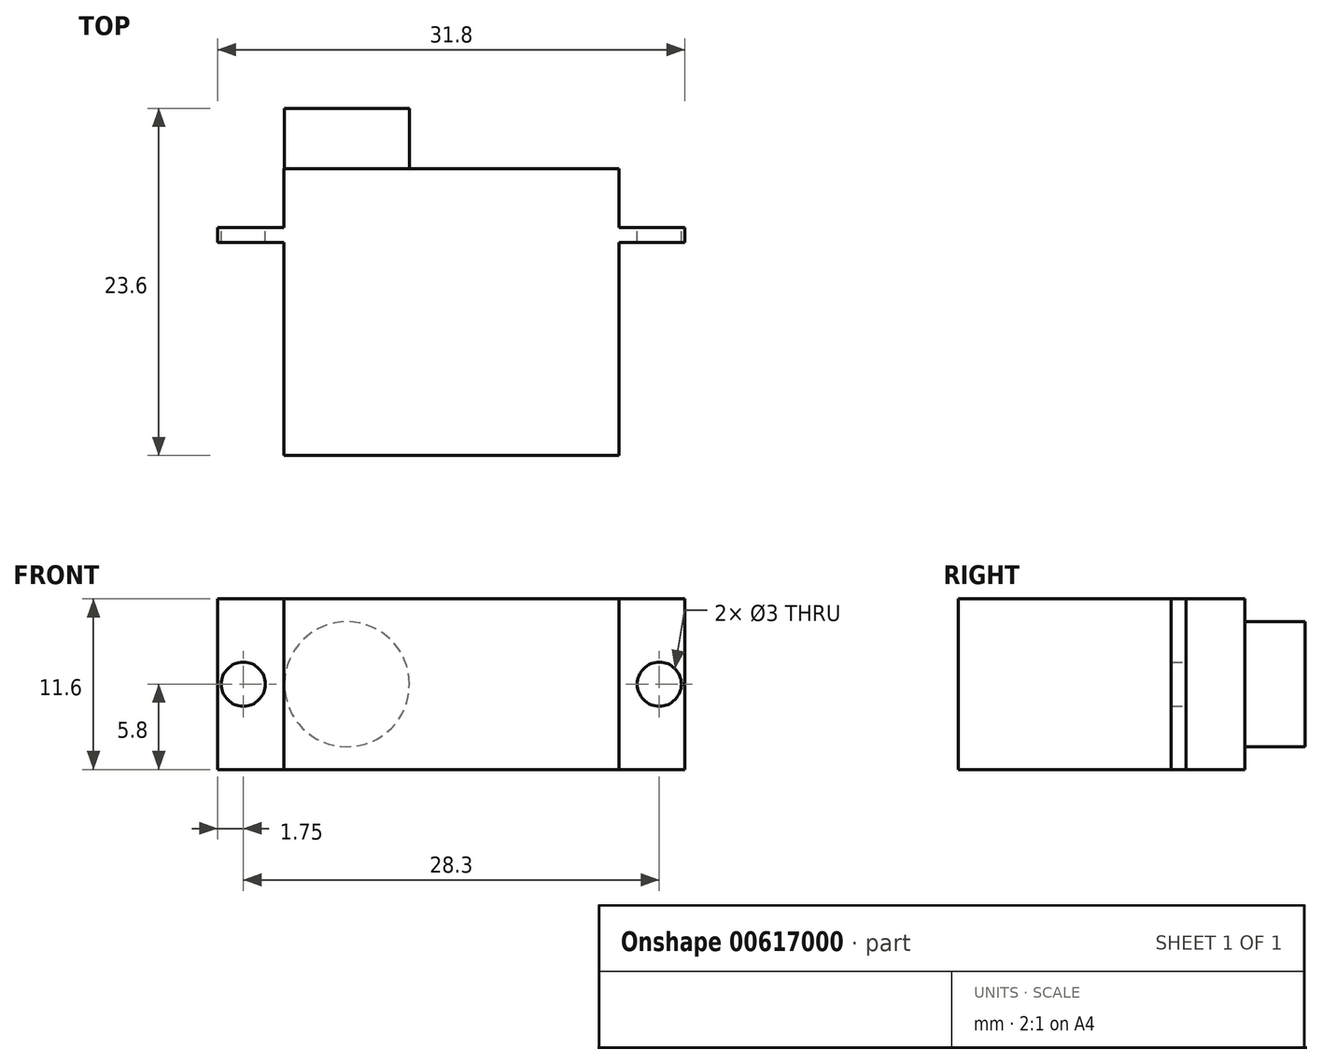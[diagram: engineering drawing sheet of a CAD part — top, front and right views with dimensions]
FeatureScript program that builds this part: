
annotation { "Feature Type Name" : "Feature", "Feature Type Description" : "" }
export const myFeature = defineFeature(function(context is Context, id is Id, definition is map)
    precondition{}
    {
        {
            var Q0;
            Q0=qCreatedBy(makeId("Top.planeOp"),FACE);
            var sketch = newSketch(context, id + "F0", { "sketchPlane" : qUnion([Q0])});
            skLineSegment(sketch, "E0.bottom", {"start": v(-11.4, 0) * mm, "end": v(11.4, 0) * mm});
            skLineSegment(sketch, "E0.top", {"start": v(-11.4, -19.5) * mm, "end": v(11.4, -19.5) * mm});
            skLineSegment(sketch, "E0.left", {"start": v(-11.4, 0) * mm, "end": v(-11.4, -19.5) * mm});
            skLineSegment(sketch, "E0.right", {"start": v(11.4, 0) * mm, "end": v(11.4, -19.5) * mm});
            skLineSegment(sketch, "E1.bottom", {"start": v(-11.4, -5) * mm, "end": v(-15.9, -5) * mm});
            skLineSegment(sketch, "E1.top", {"start": v(-11.4, -4) * mm, "end": v(-15.9, -4) * mm});
            skLineSegment(sketch, "E1.left", {"start": v(-11.4, -5) * mm, "end": v(-11.4, -4) * mm});
            skLineSegment(sketch, "E1.right", {"start": v(-15.9, -5) * mm, "end": v(-15.9, -4) * mm});
            skLineSegment(sketch, "E2.bottom", {"start": v(11.4, -5) * mm, "end": v(15.9, -5) * mm});
            skLineSegment(sketch, "E2.top", {"start": v(11.4, -4) * mm, "end": v(15.9, -4) * mm});
            skLineSegment(sketch, "E2.left", {"start": v(11.4, -5) * mm, "end": v(11.4, -4) * mm});
            skLineSegment(sketch, "E2.right", {"start": v(15.9, -5) * mm, "end": v(15.9, -4) * mm});
            skSolve(sketch);
        }
        {
            var Q0;
            Q0 = qSketchRegion(id + "F0", true);
            extrude(context, id + "F1", {"entities" : qUnion([Q0]), "endBound" : BoundingType.SYMMETRIC, "depth" : 11.6 * mm, "offsetDistance" : 25 * mm});
        }
        {
            var Q0;
            Q0=makeQuery(id+"F1.opExtrude","SWEPT_FACE",FACE,{"disambiguationData":[OSD([sQuery(id+"F0.wireOp",EDGE,"E0.bottom")])]});
            var sketch = newSketch(context, id + "F2", { "sketchPlane" : qUnion([Q0])});
            skCircle(sketch, "E3", {"center": v(7.1, 0) * mm, "radius": 4.25 * mm});
            skSolve(sketch);
        }
        {
            var Q0;
            Q0=makeQuery(id+"F2.imprint","IMPRINT",FACE,{"disambiguationData":[TD([[makeQuery(id+"F2.imprint","IMPRINT",EDGE,{"derivedFrom":sQuery(id+"F2.wireOp",EDGE,"E3")}),1.0]])]});
            extrude(context, id + "F3", {"entities" : qUnion([Q0]), "operationType" : NewBodyOperationType.ADD, "depth" : (23.6 - 19.5) * mm, "offsetDistance" : 25 * mm});
        }
        {
            var Q0;
            Q0=qCreatedBy(makeId("Front.planeOp"),FACE);
            var sketch = newSketch(context, id + "F4", { "sketchPlane" : qUnion([Q0])});
            skPoint(sketch, "E4.0", {"position": v(11.4, 0) * mm});
            skPoint(sketch, "E5", {"position": v(14.15, 0) * mm});
            skPoint(sketch, "E6.MirrorP", {"position": v(-14.15, 0) * mm});
            skSolve(sketch);
        }
        {
            var Q0;
            Q0=sQuery(id+"F4.wireOp",VERTEX,"E5");
            var Q1;
            Q1=sQuery(id+"F4.wireOp",VERTEX,"E6.MirrorP");
            var Q2;
            Q2=makeQuery(id+"F1.opExtrude","SWEPT_BODY",BODY,{"disambiguationData":[OSD([sQuery(id+"F0.wireOp",EDGE,"E0.bottom"),sQuery(id+"F0.wireOp",EDGE,"E0.top"),sQuery(id+"F0.wireOp",EDGE,"E0.left"),sQuery(id+"F0.wireOp",EDGE,"E0.right"),sQuery(id+"F0.wireOp",EDGE,"E1.bottom"),sQuery(id+"F0.wireOp",EDGE,"E1.top"),sQuery(id+"F0.wireOp",EDGE,"E1.right"),sQuery(id+"F0.wireOp",EDGE,"E2.bottom"),sQuery(id+"F0.wireOp",EDGE,"E2.top"),sQuery(id+"F0.wireOp",EDGE,"E2.right")])]});
            hole(context, id + "F5", {"style" : HoleStyle.SIMPLE, "endStyle" : HoleEndStyle.THROUGH, "oppositeDirection" : true, "holeDiameter" : 3 * mm, "majorDiameter" : 5 * mm, "isTappedThrough" : true, "tappedDepth" : 6 * mm, "tapClearance" : 3, "locations" : qUnion([Q0, Q1]), "scope" : qUnion([Q2])});
        }
    });
